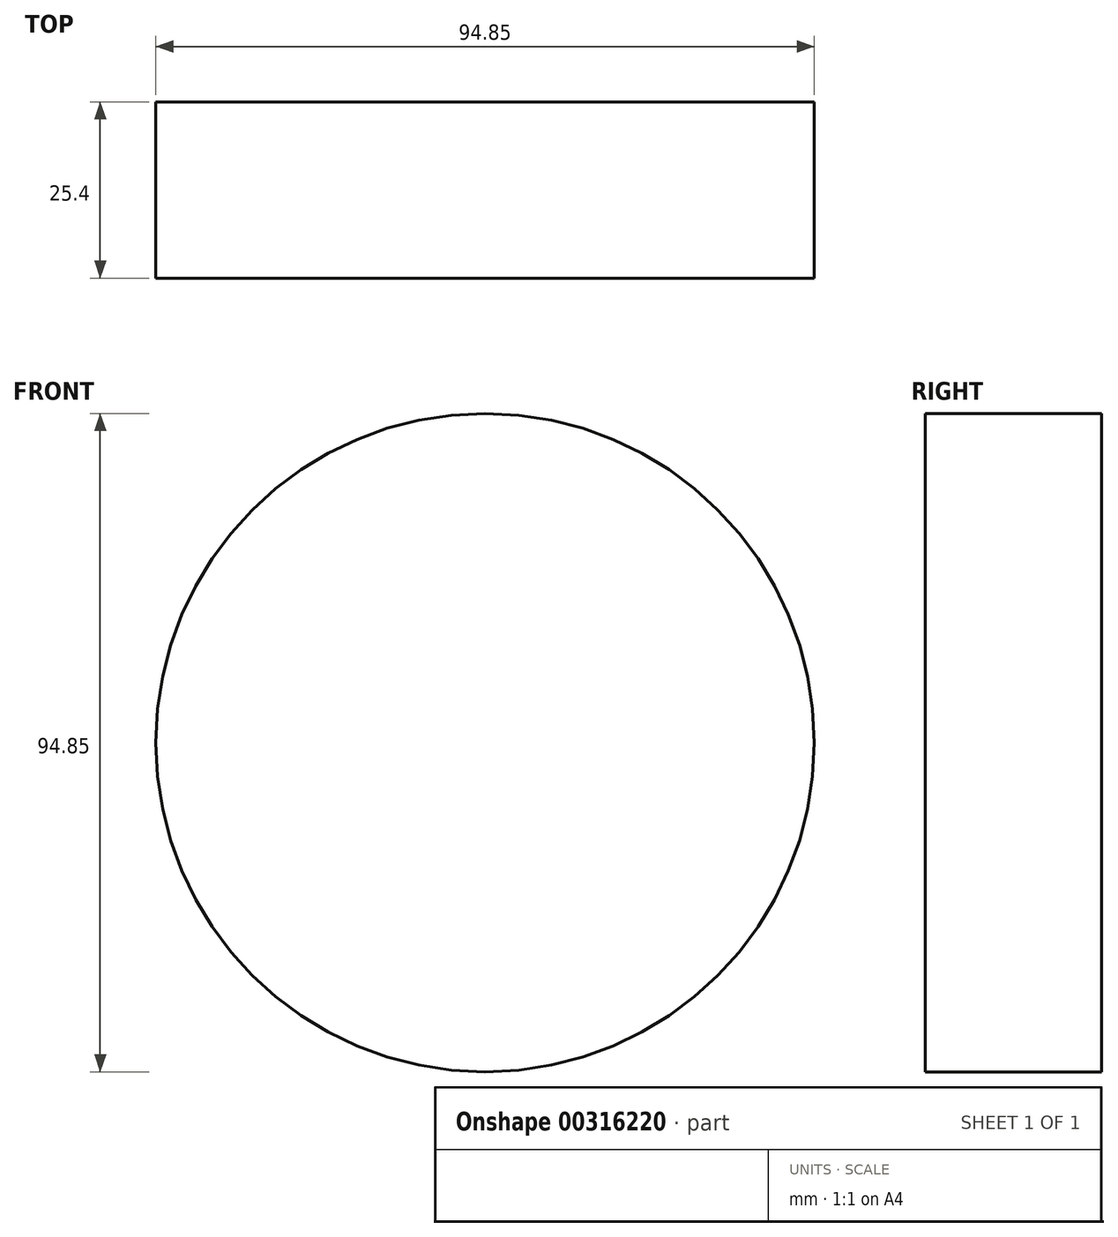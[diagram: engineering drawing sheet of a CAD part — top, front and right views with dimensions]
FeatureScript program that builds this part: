
annotation { "Feature Type Name" : "Feature", "Feature Type Description" : "" }
export const myFeature = defineFeature(function(context is Context, id is Id, definition is map)
    precondition{}
    {
        {
            var Q0;
            Q0=qCreatedBy(makeId("Front.planeOp"),FACE);
            var sketch = newSketch(context, id + "F0", { "sketchPlane" : qUnion([Q0])});
            skCircle(sketch, "E0", {"center": v(49.39, -3.75) * mm, "radius": 66.51 * mm});
            skCircle(sketch, "E1", {"center": v(49.39, -3.75) * mm, "radius": 47.43 * mm});
            skSolve(sketch);
        }
        {
            var Q0;
            Q0=makeQuery(id+"F0.imprint","IMPRINT",FACE,{"disambiguationData":[TD([[makeQuery(id+"F0.imprint","IMPRINT",EDGE,{"derivedFrom":sQuery(id+"F0.wireOp",EDGE,"E1")}),1.0]])]});
            extrude(context, id + "F1", {"entities" : qUnion([Q0]), "endBound" : BoundingType.SYMMETRIC, "depth" : 25.4 * mm});
        }
    });
